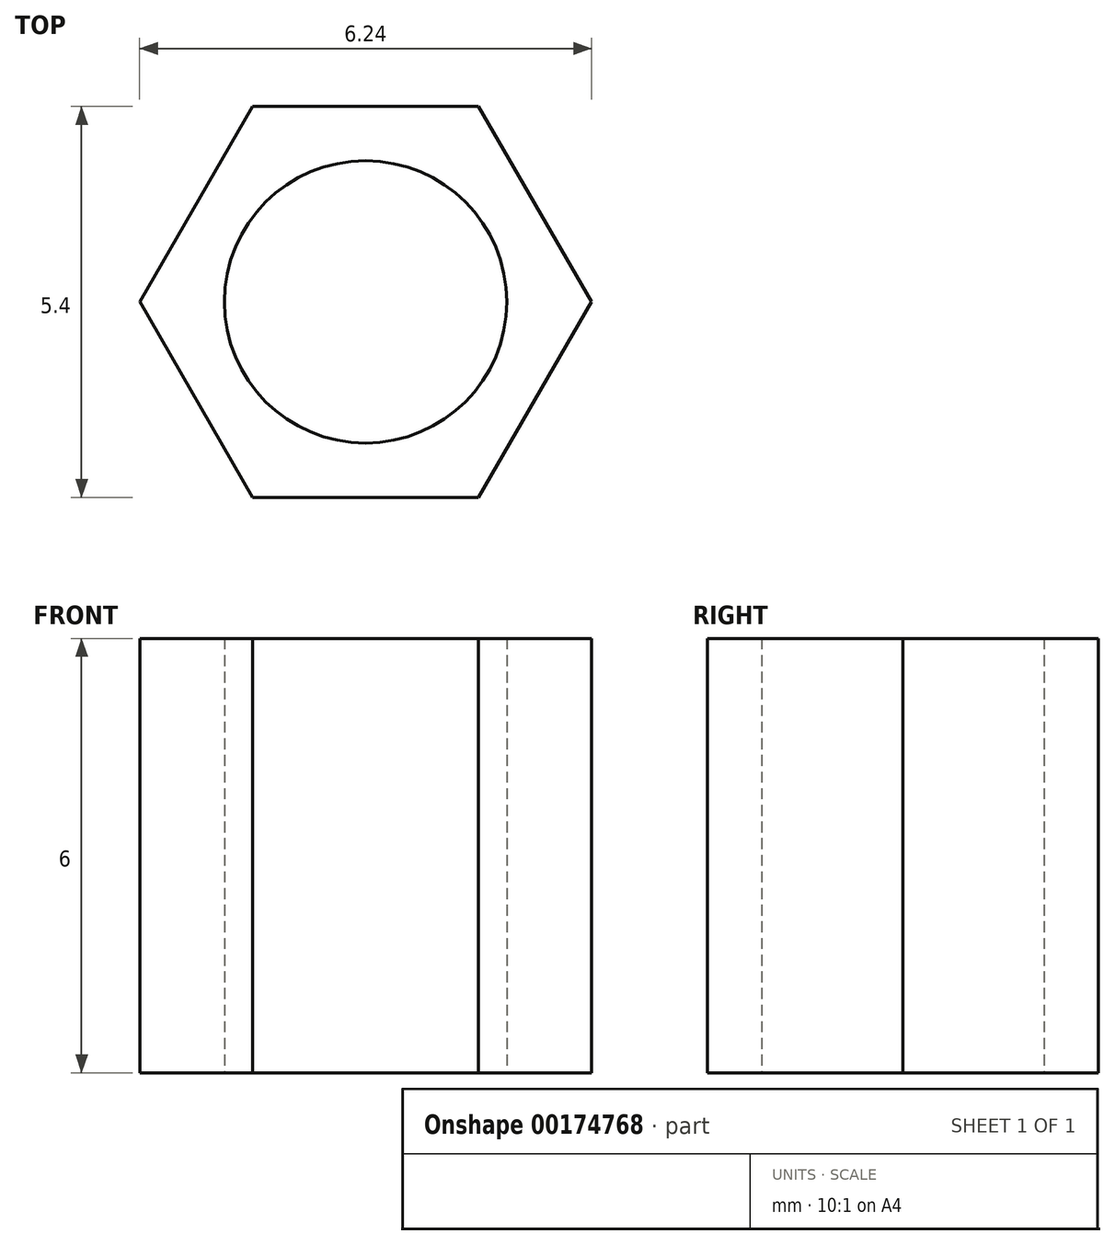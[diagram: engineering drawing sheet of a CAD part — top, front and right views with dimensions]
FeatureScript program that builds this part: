
annotation { "Feature Type Name" : "Feature", "Feature Type Description" : "" }
export const myFeature = defineFeature(function(context is Context, id is Id, definition is map)
    precondition{}
    {
        {
            var Q0;
            Q0=qCreatedBy(makeId("Top.planeOp"),FACE);
            var sketch = newSketch(context, id + "F0", { "sketchPlane" : qUnion([Q0])});
            skCircle(sketch, "E0.cCircle", {"center": v(0, 0) * mm, "radius": 2.7 * mm, "construction": true});
            skLineSegment(sketch, "E0.0", {"start": v(-1.56, 2.7) * mm, "end": v(1.56, 2.7) * mm});
            skLineSegment(sketch, "E0.1", {"start": v(1.56, 2.7) * mm, "end": v(3.12, 0) * mm});
            skLineSegment(sketch, "E0.2", {"start": v(3.12, 0) * mm, "end": v(1.56, -2.7) * mm});
            skLineSegment(sketch, "E0.3", {"start": v(1.56, -2.7) * mm, "end": v(-1.56, -2.7) * mm});
            skLineSegment(sketch, "E0.4", {"start": v(-1.56, -2.7) * mm, "end": v(-3.12, 0) * mm});
            skLineSegment(sketch, "E0.5", {"start": v(-3.12, 0) * mm, "end": v(-1.56, 2.7) * mm});
            skPoint(sketch, "E0.0.midPoint", {"position": v(0, 2.7) * mm});
            skCircle(sketch, "E1", {"center": v(0, 0) * mm, "radius": 1.95 * mm});
            skSolve(sketch);
        }
        {
            var Q0;
            Q0=qSketchRegion(id+"F0",true);
            extrude(context, id + "F1", {"entities" : qUnion([Q0]), "depth" : 6 * mm});
        }
    });
